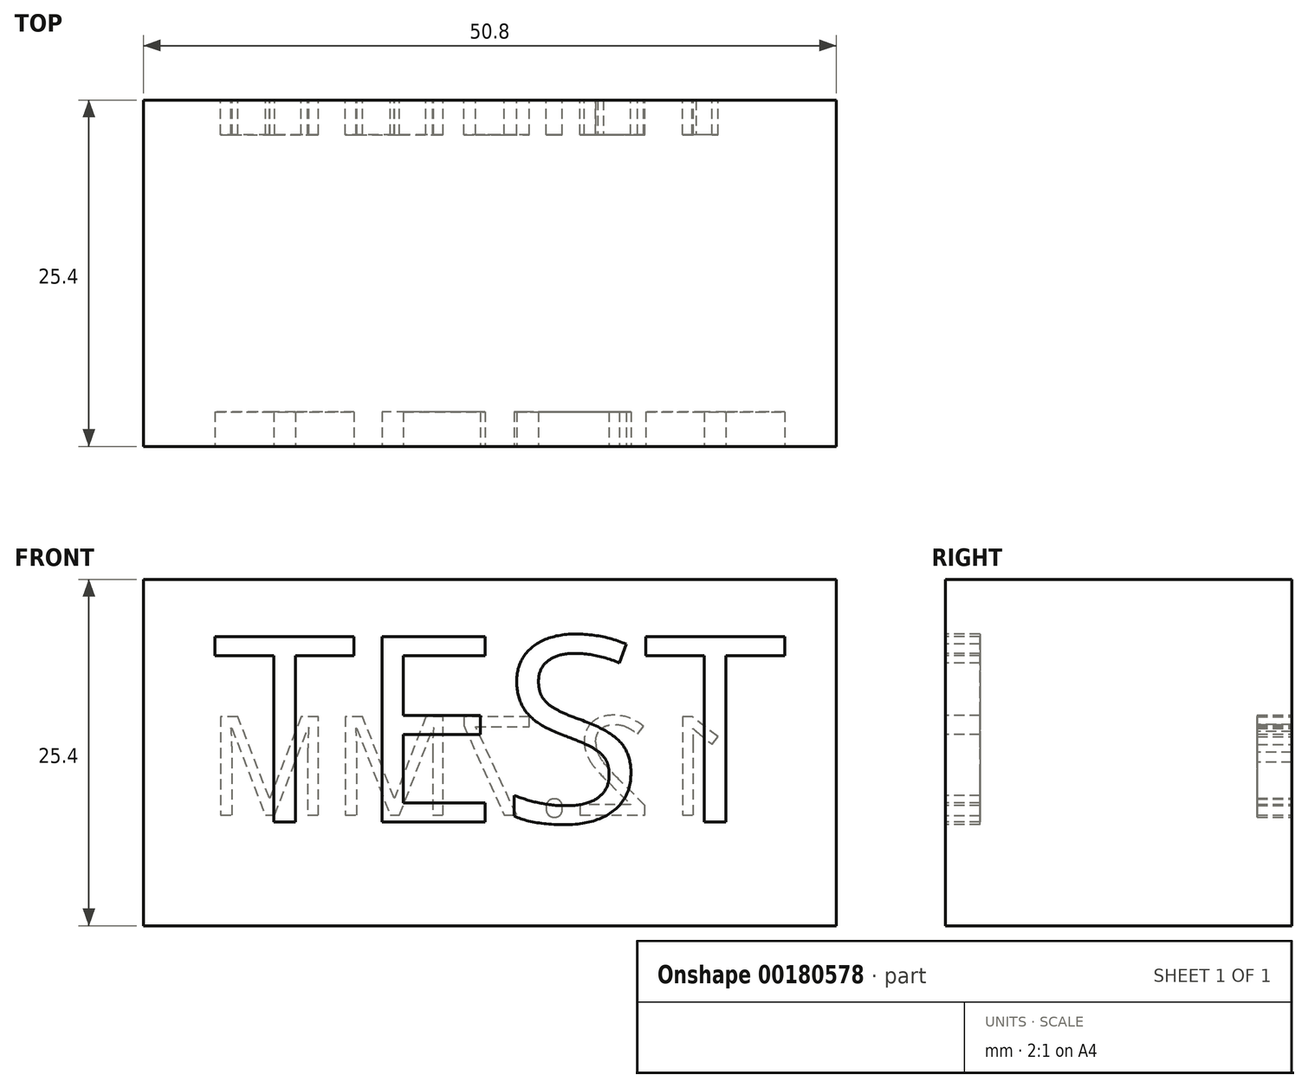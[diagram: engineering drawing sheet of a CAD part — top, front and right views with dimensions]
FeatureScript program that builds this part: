
annotation { "Feature Type Name" : "Feature", "Feature Type Description" : "" }
export const myFeature = defineFeature(function(context is Context, id is Id, definition is map)
    precondition{}
    {
        {
            var Q0;
            Q0=qCreatedBy(makeId("Top.planeOp"),FACE);
            var sketch = newSketch(context, id + "F0", { "sketchPlane" : qUnion([Q0])});
            skLineSegment(sketch, "E0.bottom", {"start": v(25.4, -12.7) * mm, "end": v(-25.4, -12.7) * mm});
            skLineSegment(sketch, "E0.top", {"start": v(25.4, 12.7) * mm, "end": v(-25.4, 12.7) * mm});
            skLineSegment(sketch, "E0.left", {"start": v(25.4, -12.7) * mm, "end": v(25.4, 12.7) * mm});
            skLineSegment(sketch, "E0.right", {"start": v(-25.4, -12.7) * mm, "end": v(-25.4, 12.7) * mm});
            skPoint(sketch, "E0.middle", {"position": v(0, 0) * mm});
            skSolve(sketch);
        }
        {
            var Q0;
            Q0 = qSketchRegion(id + "F0", true);
            extrude(context, id + "F1", {"entities" : qUnion([Q0]), "depth" : 25.4 * mm});
        }
        {
            var Q0;
            Q0=makeQuery(id+"F1.opExtrude","SWEPT_FACE",FACE,{"disambiguationData":[OSD([sQuery(id+"F0.wireOp",EDGE,"E0.bottom")])]});
            var sketch = newSketch(context, id + "F2", { "sketchPlane" : qUnion([Q0])});
            skText(sketch, "E1", { "text": "TEST", "fontName": "OpenSans-Regular.ttf"});
            const initialGuessF2  = {"E1": [-0.02032, 0.0076, 1, 0, 0.01371]};
            skSetInitialGuess(sketch, initialGuessF2);
            skSolve(sketch);
        }
        {
            var Q0;
            Q0 = qSketchRegion(id + "F2", true);
            extrude(context, id + "F3", {"entities" : qUnion([Q0]), "operationType" : NewBodyOperationType.REMOVE, "oppositeDirection" : true, "depth" : 2.54 * mm});
        }
        {
            var Q0;
            Q0=makeQuery(id+"F1.opExtrude","SWEPT_FACE",FACE,{"disambiguationData":[OSD([sQuery(id+"F0.wireOp",EDGE,"E0.top")])]});
            var sketch = newSketch(context, id + "F4", { "sketchPlane" : qUnion([Q0])});
            skText(sketch, "E2", { "text": "12.7MM", "fontName": "OpenSans-Regular.ttf"});
            const initialGuessF4  = {"E2": [-0.01766, 0.0081, 1, 0, 0.0073]};
            skSetInitialGuess(sketch, initialGuessF4);
            skSolve(sketch);
        }
        {
            var Q0;
            Q0 = qSketchRegion(id + "F4", true);
            extrude(context, id + "F5", {"entities" : qUnion([Q0]), "operationType" : NewBodyOperationType.REMOVE, "oppositeDirection" : true, "depth" : 2.54 * mm});
        }
    });
